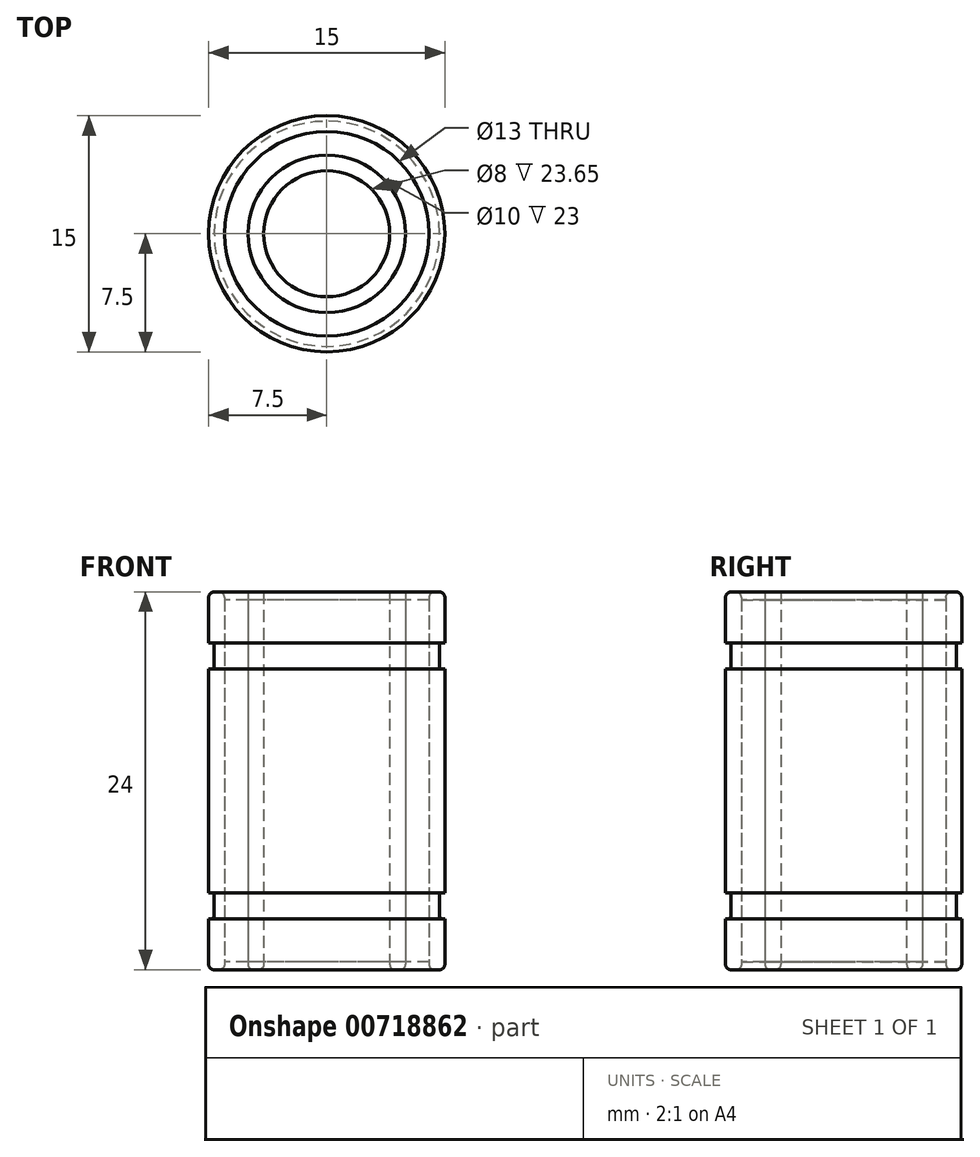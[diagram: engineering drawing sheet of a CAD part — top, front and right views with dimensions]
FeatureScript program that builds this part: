
annotation { "Feature Type Name" : "Feature", "Feature Type Description" : "" }
export const myFeature = defineFeature(function(context is Context, id is Id, definition is map)
    precondition{}
    {
        {
            var Q0;
            Q0=qCreatedBy(makeId("Top.planeOp"),FACE);
            cPlane(context, id + "F0", {"entities" : qUnion([Q0]), "cplaneType" : CPlaneType.OFFSET, "offset" : 24 * mm, "width" : 150 * mm, "height" : 150 * mm});
        }
        {
            var Q0;
            Q0=qCreatedBy(makeId("Top.planeOp"),FACE);
            var sketch = newSketch(context, id + "F1", { "sketchPlane" : qUnion([Q0])});
            skCircle(sketch, "E0", {"center": v(0, 0) * mm, "radius": 7.5 * mm});
            skCircle(sketch, "E1", {"center": v(0, 0) * mm, "radius": 6.5 * mm});
            skSolve(sketch);
        }
        {
            var Q0;
            Q0=makeQuery(id+"F1.imprint","IMPRINT",FACE,{"disambiguationData":[TD([[makeQuery(id+"F1.imprint","IMPRINT",EDGE,{"derivedFrom":sQuery(id+"F1.wireOp",EDGE,"E0")}),1.0]])]});
            var Q1;
            Q1=qCreatedBy(id+"F0.planeOp",FACE);
            extrude(context, id + "F2", {"entities" : qUnion([Q0]), "endBound" : BoundingType.UP_TO_SURFACE, "depth" : 24 * mm, "endBoundEntityFace" : qUnion([Q1]), "offsetDistance" : 25 * mm});
        }
        {
            var Q0;
            Q0=qCreatedBy(makeId("Top.planeOp"),FACE);
            var sketch = newSketch(context, id + "F3", { "sketchPlane" : qUnion([Q0])});
            skCircle(sketch, "E2", {"center": v(0, 0) * mm, "radius": 4 * mm});
            skCircle(sketch, "E3.0", {"center": v(0, 0) * mm, "radius": 5 * mm});
            skSolve(sketch);
        }
        {
            var Q0;
            Q0 = qSketchRegion(id + "F3", true);
            var Q1;
            Q1=qCreatedBy(id+"F0.planeOp",FACE);
            extrude(context, id + "F4", {"entities" : qUnion([Q0]), "endBound" : BoundingType.UP_TO_SURFACE, "depth" : 25 * mm, "endBoundEntityFace" : qUnion([Q1]), "offsetDistance" : 25 * mm});
        }
        {
            var Q0;
            Q0=makeQuery(id+"F2.opExtrude","CAP_EDGE",EDGE,{"disambiguationData":[OSD([sQuery(id+"F1.wireOp",EDGE,"E0")])],"isStart":false});
            var Q1;
            Q1=makeQuery(id+"F2.opExtrude","CAP_EDGE",EDGE,{"disambiguationData":[OSD([sQuery(id+"F1.wireOp",EDGE,"E0")])],"isStart":true});
            var Q2;
            Q2=makeQuery(id+"F2.opExtrude","CAP_EDGE",EDGE,{"disambiguationData":[OSD([sQuery(id+"F1.wireOp",EDGE,"E1")])],"isStart":false});
            var Q3;
            Q3=makeQuery(id+"F2.opExtrude","CAP_EDGE",EDGE,{"disambiguationData":[OSD([sQuery(id+"F1.wireOp",EDGE,"E1")])],"isStart":true});
            var Q4;
            Q4=makeQuery(id+"F2.opExtrude","TWEAK_EDGE",EDGE,{"derivedFrom":[dummyQuery(id+"F0.planeOp",FACE),makeQuery(id+"F1.imprint","IMPRINT",EDGE,{"derivedFrom":sQuery(id+"F1.wireOp",EDGE,"E1")})]});
            var Q5;
            Q5=makeQuery(id+"F2.opExtrude","TWEAK_EDGE",EDGE,{"derivedFrom":[dummyQuery(id+"F0.planeOp",FACE),makeQuery(id+"F1.imprint","IMPRINT",EDGE,{"derivedFrom":sQuery(id+"F1.wireOp",EDGE,"E0")})]});
            var Q6;
            Q6=makeQuery(id+"F4.opExtrude","TWEAK_EDGE",EDGE,{"derivedFrom":[dummyQuery(id+"F0.planeOp",FACE),makeQuery(id+"F3.imprint","IMPRINT",EDGE,{"derivedFrom":sQuery(id+"F3.wireOp",EDGE,"E2")})]});
            var Q7;
            Q7=makeQuery(id+"F4.opExtrude","TWEAK_EDGE",EDGE,{"derivedFrom":[dummyQuery(id+"F0.planeOp",FACE),makeQuery(id+"F3.imprint","IMPRINT",EDGE,{"derivedFrom":sQuery(id+"F3.wireOp",EDGE,"E3.0")})]});
            var Q8;
            Q8=makeQuery(id+"F4.opExtrude","CAP_EDGE",EDGE,{"disambiguationData":[OSD([sQuery(id+"F3.wireOp",EDGE,"E3.0")])],"isStart":true});
            var Q9;
            Q9=makeQuery(id+"F4.opExtrude","CAP_EDGE",EDGE,{"disambiguationData":[OSD([sQuery(id+"F3.wireOp",EDGE,"E2")])],"isStart":true});
            fillet(context, id + "F5", {"entities" : qUnion([Q0, Q1, Q2, Q3, Q4, Q5, Q6, Q7, Q8, Q9]), "radius" : 0.35 * mm, "tangentPropagation" : true, "allowEdgeOverflow" : false});
        }
        {
            var Q0;
            Q0=qCreatedBy(makeId("Top.planeOp"),FACE);
            var sketch = newSketch(context, id + "F6", { "sketchPlane" : qUnion([Q0])});
            skCircle(sketch, "E4", {"center": v(0, 0) * mm, "radius": 6.5 * mm});
            skCircle(sketch, "E5", {"center": v(0, 0) * mm, "radius": 5 * mm});
            skSolve(sketch);
        }
        {
            var Q0;
            Q0 = qSketchRegion(id + "F6", true);
            var Q1;
            Q1=qCreatedBy(id+"F0.planeOp",FACE);
            var Q2;
            Q2=qCreatedBy(id+"F0.planeOp",FACE);
            extrude(context, id + "F7", {"entities" : qUnion([Q0]), "endBound" : BoundingType.UP_TO_SURFACE, "depth" : 0.75 * mm, "endBoundEntityFace" : qUnion([Q1]), "hasOffset" : true, "offsetDistance" : 0.5 * mm, "hasSecondDirection" : true, "secondDirectionBound" : SecondDirectionBoundingType.UP_TO_SURFACE, "secondDirectionOppositeDirection" : false, "secondDirectionDepth" : 25 * mm, "secondDirectionBoundEntityFace" : qUnion([Q2]), "hasSecondDirectionOffset" : true, "secondDirectionOffsetDistance" : 23.5 * mm});
        }
        {
            var Q0;
            Q0=qCreatedBy(makeId("Front.planeOp"),FACE);
            var sketch = newSketch(context, id + "F8", { "sketchPlane" : qUnion([Q0])});
            skLineSegment(sketch, "E6.bottom", {"start": v(7.15, 20.75) * mm, "end": v(11.46, 20.75) * mm});
            skLineSegment(sketch, "E6.top", {"start": v(7.15, 19.11) * mm, "end": v(11.46, 19.11) * mm});
            skLineSegment(sketch, "E6.left", {"start": v(7.15, 20.75) * mm, "end": v(7.15, 19.11) * mm});
            skLineSegment(sketch, "E6.right", {"start": v(11.46, 20.75) * mm, "end": v(11.46, 19.11) * mm});
            skLineSegment(sketch, "E7", {"start": v(-31.16, 12) * mm, "end": v(26.68, 12) * mm});
            skLineSegment(sketch, "E8.MirrorCS", {"start": v(7.15, 3.25) * mm, "end": v(11.46, 3.25) * mm});
            skLineSegment(sketch, "E9.MirrorCS", {"start": v(7.15, 4.89) * mm, "end": v(11.46, 4.89) * mm});
            skLineSegment(sketch, "E10.MirrorCS", {"start": v(7.15, 3.25) * mm, "end": v(7.15, 4.89) * mm});
            skLineSegment(sketch, "E11.MirrorCS", {"start": v(11.46, 3.25) * mm, "end": v(11.46, 4.89) * mm});
            skSolve(sketch);
        }
        {
            var Q0;
            Q0=makeQuery(id+"F8.imprint","IMPRINT",FACE,{"disambiguationData":[TD([[makeQuery(id+"F8.imprint","IMPRINT",EDGE,{"derivedFrom":sQuery(id+"F8.wireOp",EDGE,"E6.bottom")}),-1.0]])]});
            var Q1;
            Q1=makeQuery(id+"F8.imprint","IMPRINT",FACE,{"disambiguationData":[TD([[makeQuery(id+"F8.imprint","IMPRINT",EDGE,{"derivedFrom":sQuery(id+"F8.wireOp",EDGE,"E8.MirrorCS")}),1.0]])]});
            var Q2;
            Q2=makeQuery(id+"F4.opExtrude","SWEPT_FACE",FACE,{"disambiguationData":[OSD([sQuery(id+"F3.wireOp",EDGE,"E2")])]});
            revolve(context, id + "F9", {"operationType" : NewBodyOperationType.REMOVE, "surfaceOperationType" : NewSurfaceOperationType.NEW, "entities" : qUnion([Q0, Q1]), "axis" : qUnion([Q2]), "revolveType" : RevolveType.FULL, "oppositeDirection" : true});
        }
        {
            var Q0;
            Q0=makeQuery(id+"F9.boolean.opBoolean","COPY",EDGE,{"derivedFrom":makeQuery(id+"F9.opRevolve","SWEPT_EDGE",EDGE,{"disambiguationData":[OSD([sQuery(id+"F8.wireOp",EDGE,"E6.bottom"),sQuery(id+"F8.wireOp",EDGE,"E6.left")])]})});
            var Q1;
            Q1=makeQuery(id+"F9.boolean.opBoolean","COPY",EDGE,{"derivedFrom":makeQuery(id+"F9.opRevolve","SWEPT_EDGE",EDGE,{"disambiguationData":[OSD([sQuery(id+"F8.wireOp",EDGE,"E6.top"),sQuery(id+"F8.wireOp",EDGE,"E6.left")])]})});
            var Q2;
            Q2=makeQuery(id+"F9.boolean.opBoolean","COPY",EDGE,{"derivedFrom":makeQuery(id+"F9.opRevolve","SWEPT_EDGE",EDGE,{"disambiguationData":[OSD([sQuery(id+"F8.wireOp",EDGE,"E8.MirrorCS"),sQuery(id+"F8.wireOp",EDGE,"E10.MirrorCS")])]})});
            var Q3;
            Q3=makeQuery(id+"F9.boolean.opBoolean","COPY",EDGE,{"derivedFrom":makeQuery(id+"F9.opRevolve","SWEPT_EDGE",EDGE,{"disambiguationData":[OSD([sQuery(id+"F8.wireOp",EDGE,"E9.MirrorCS"),sQuery(id+"F8.wireOp",EDGE,"E10.MirrorCS")])]})});
            fillet(context, id + "F10", {"entities" : qUnion([Q0, Q1, Q2, Q3]), "radius" : 0.15 * mm, "tangentPropagation" : true, "allowEdgeOverflow" : false});
        }
    });
